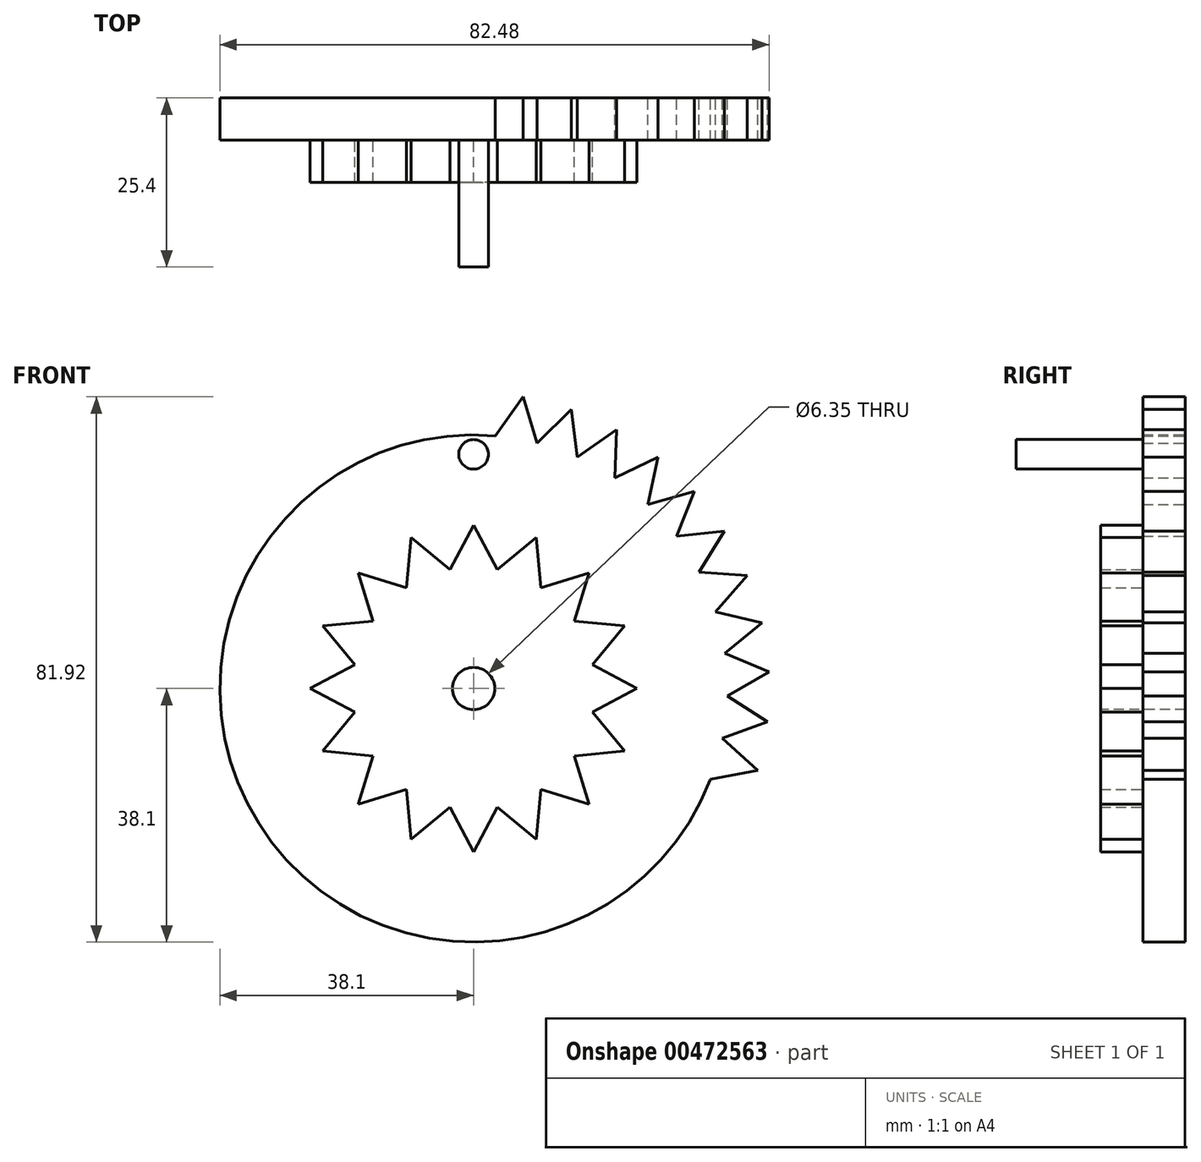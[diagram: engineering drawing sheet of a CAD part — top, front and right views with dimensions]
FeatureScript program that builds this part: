
annotation { "Feature Type Name" : "Feature", "Feature Type Description" : "" }
export const myFeature = defineFeature(function(context is Context, id is Id, definition is map)
    precondition{}
    {
        {
            var Q0;
            Q0=qCreatedBy(makeId("Front.planeOp"),FACE);
            var sketch = newSketch(context, id + "F0", { "sketchPlane" : qUnion([Q0])});
            skCircle(sketch, "E0", {"center": v(0, 0) * mm, "radius": 38.1 * mm});
            skPoint(sketch, "E1", {"position": v(0, 38.1) * mm});
            skPoint(sketch, "E2.1.0", {"position": v(6.38, 37.56) * mm});
            skPoint(sketch, "E2.2.0", {"position": v(12.58, 35.96) * mm});
            skPoint(sketch, "E2.3.0", {"position": v(18.43, 33.35) * mm});
            skPoint(sketch, "E2.4.0", {"position": v(23.75, 29.79) * mm});
            skPoint(sketch, "E2.5.0", {"position": v(28.4, 25.39) * mm});
            skPoint(sketch, "E2.6.0", {"position": v(32.26, 20.27) * mm});
            skPoint(sketch, "E2.7.0", {"position": v(35.2, 14.58) * mm});
            skPoint(sketch, "E2.8.0", {"position": v(37.14, 8.48) * mm});
            skPoint(sketch, "E2.9.0", {"position": v(38.04, 2.14) * mm});
            skPoint(sketch, "E2.10.0", {"position": v(37.86, -4.27) * mm});
            skPoint(sketch, "E2.11.0", {"position": v(36.61, -10.55) * mm});
            skPoint(sketch, "E2.12.0", {"position": v(34.33, -16.53) * mm});
            skPoint(sketch, "E2.13.0", {"position": v(31.07, -22.05) * mm});
            skPoint(sketch, "E2.14.0", {"position": v(26.94, -26.94) * mm});
            skPoint(sketch, "E2.15.0", {"position": v(22.05, -31.07) * mm});
            skPoint(sketch, "E2.16.0", {"position": v(16.53, -34.33) * mm});
            skPoint(sketch, "E2.17.0", {"position": v(10.55, -36.61) * mm});
            skPoint(sketch, "E2.18.0", {"position": v(4.27, -37.86) * mm});
            skPoint(sketch, "E2.19.0", {"position": v(-2.14, -38.04) * mm});
            skPoint(sketch, "E2.20.0", {"position": v(-8.48, -37.14) * mm});
            skPoint(sketch, "E2.21.0", {"position": v(-14.58, -35.2) * mm});
            skPoint(sketch, "E2.22.0", {"position": v(-20.27, -32.26) * mm});
            skPoint(sketch, "E2.23.0", {"position": v(-25.39, -28.4) * mm});
            skPoint(sketch, "E2.24.0", {"position": v(-29.79, -23.75) * mm});
            skPoint(sketch, "E2.25.0", {"position": v(-33.35, -18.43) * mm});
            skPoint(sketch, "E2.26.0", {"position": v(-35.96, -12.58) * mm});
            skPoint(sketch, "E2.27.0", {"position": v(-37.56, -6.38) * mm});
            skLineSegment(sketch, "E2.anchor1", {"start": v(0, 0) * mm, "end": v(0, 38.1) * mm, "construction": true});
            skLineSegment(sketch, "E2.anchor2", {"start": v(0, 0) * mm, "end": v(-38.1, 0) * mm, "construction": true});
            skPoint(sketch, "E3.0.28.0", {"position": v(-38.1, 0) * mm});
            skPoint(sketch, "E4", {"position": v(-3.17, 37.97) * mm});
            skPoint(sketch, "E5.1.0", {"position": v(3.23, 37.96) * mm});
            skPoint(sketch, "E5.2.0", {"position": v(9.55, 36.88) * mm});
            skPoint(sketch, "E5.3.0", {"position": v(15.59, 34.76) * mm});
            skPoint(sketch, "E5.4.0", {"position": v(21.2, 31.66) * mm});
            skPoint(sketch, "E5.5.0", {"position": v(26.2, 27.67) * mm});
            skPoint(sketch, "E5.6.0", {"position": v(30.46, 22.89) * mm});
            skPoint(sketch, "E5.7.0", {"position": v(33.86, 17.46) * mm});
            skPoint(sketch, "E5.8.0", {"position": v(36.3, 11.54) * mm});
            skPoint(sketch, "E5.9.0", {"position": v(37.73, 5.3) * mm});
            skPoint(sketch, "E5.10.0", {"position": v(38.08, -1.1) * mm});
            skPoint(sketch, "E5.11.0", {"position": v(37.36, -7.46) * mm});
            skPoint(sketch, "E5.12.0", {"position": v(35.58, -13.62) * mm});
            skPoint(sketch, "E5.13.0", {"position": v(32.8, -19.38) * mm});
            skPoint(sketch, "E5.14.0", {"position": v(29.1, -24.6) * mm});
            skPoint(sketch, "E5.15.0", {"position": v(24.56, -29.13) * mm});
            skPoint(sketch, "E5.16.0", {"position": v(19.33, -32.83) * mm});
            skPoint(sketch, "E5.17.0", {"position": v(13.56, -35.6) * mm});
            skPoint(sketch, "E5.18.0", {"position": v(7.4, -37.37) * mm});
            skPoint(sketch, "E5.19.0", {"position": v(1.04, -38.09) * mm});
            skPoint(sketch, "E5.20.0", {"position": v(-5.36, -37.72) * mm});
            skPoint(sketch, "E5.21.0", {"position": v(-11.6, -36.3) * mm});
            skPoint(sketch, "E5.22.0", {"position": v(-17.51, -33.84) * mm});
            skPoint(sketch, "E5.23.0", {"position": v(-22.93, -30.42) * mm});
            skPoint(sketch, "E5.24.0", {"position": v(-27.7, -26.15) * mm});
            skPoint(sketch, "E5.25.0", {"position": v(-31.7, -21.14) * mm});
            skPoint(sketch, "E5.26.0", {"position": v(-34.79, -15.53) * mm});
            skPoint(sketch, "E5.27.0", {"position": v(-36.9, -9.49) * mm});
            skPoint(sketch, "E5.28.0", {"position": v(-37.97, -3.17) * mm});
            skLineSegment(sketch, "E5.anchor1", {"start": v(0, 0) * mm, "end": v(-3.17, 37.97) * mm, "construction": true});
            skLineSegment(sketch, "E5.anchor2", {"start": v(0, 0) * mm, "end": v(-37.97, -3.17) * mm, "construction": true});
            skLineSegment(sketch, "E6", {"start": v(6.38, 37.56) * mm, "end": v(0, 0) * mm});
            skLineSegment(sketch, "E7", {"start": v(12.58, 35.96) * mm, "end": v(0, 0) * mm});
            skLineSegment(sketch, "E8", {"start": v(18.43, 33.35) * mm, "end": v(0, 0) * mm});
            skLineSegment(sketch, "E9", {"start": v(23.75, 29.79) * mm, "end": v(0, 0) * mm});
            skLineSegment(sketch, "E10", {"start": v(28.4, 25.39) * mm, "end": v(0, 0) * mm});
            skLineSegment(sketch, "E11", {"start": v(32.26, 20.27) * mm, "end": v(0, 0) * mm});
            skLineSegment(sketch, "E12", {"start": v(35.2, 14.58) * mm, "end": v(0, 0) * mm});
            skLineSegment(sketch, "E13", {"start": v(37.14, 8.48) * mm, "end": v(0, 0) * mm});
            skLineSegment(sketch, "E14", {"start": v(38.04, 2.14) * mm, "end": v(0, 0) * mm});
            skLineSegment(sketch, "E15", {"start": v(37.86, -4.27) * mm, "end": v(0, 0) * mm});
            skLineSegment(sketch, "E16", {"start": v(36.61, -10.55) * mm, "end": v(0, 0) * mm});
            skLineSegment(sketch, "E17", {"start": v(34.33, -16.53) * mm, "end": v(0, 0) * mm});
            skLineSegment(sketch, "E18", {"start": v(31.07, -22.05) * mm, "end": v(0, 0) * mm});
            skLineSegment(sketch, "E19", {"start": v(26.94, -26.94) * mm, "end": v(0, 0) * mm});
            skLineSegment(sketch, "E20", {"start": v(22.05, -31.07) * mm, "end": v(0, 0) * mm});
            skLineSegment(sketch, "E21", {"start": v(16.53, -34.33) * mm, "end": v(0, 0) * mm});
            skLineSegment(sketch, "E22", {"start": v(10.55, -36.61) * mm, "end": v(0, 0) * mm});
            skLineSegment(sketch, "E23", {"start": v(4.27, -37.86) * mm, "end": v(0, 0) * mm});
            skLineSegment(sketch, "E24", {"start": v(-2.14, -38.04) * mm, "end": v(0, 0) * mm});
            skLineSegment(sketch, "E25", {"start": v(-8.48, -37.14) * mm, "end": v(0, 0) * mm});
            skLineSegment(sketch, "E26", {"start": v(-14.58, -35.2) * mm, "end": v(0, 0) * mm});
            skLineSegment(sketch, "E27", {"start": v(-20.27, -32.26) * mm, "end": v(0, 0) * mm});
            skLineSegment(sketch, "E28", {"start": v(-25.39, -28.4) * mm, "end": v(0, 0) * mm});
            skLineSegment(sketch, "E29", {"start": v(-29.79, -23.75) * mm, "end": v(0, 0) * mm});
            skLineSegment(sketch, "E30", {"start": v(-33.35, -18.43) * mm, "end": v(0, 0) * mm});
            skLineSegment(sketch, "E31", {"start": v(-35.96, -12.58) * mm, "end": v(0, 0) * mm});
            skLineSegment(sketch, "E32", {"start": v(-37.56, -6.38) * mm, "end": v(0, 0) * mm});
            skLineSegment(sketch, "E33", {"start": v(0, 38.1) * mm, "end": v(0, 44.45) * mm});
            skLineSegment(sketch, "E34", {"start": v(6.38, 37.56) * mm, "end": v(7.45, 43.82) * mm});
            skLineSegment(sketch, "E35", {"start": v(12.58, 35.96) * mm, "end": v(14.68, 41.96) * mm});
            skLineSegment(sketch, "E36", {"start": v(18.43, 33.35) * mm, "end": v(21.5, 38.9) * mm});
            skLineSegment(sketch, "E37", {"start": v(23.75, 29.79) * mm, "end": v(27.71, 34.75) * mm});
            skLineSegment(sketch, "E38", {"start": v(28.4, 25.39) * mm, "end": v(33.14, 29.62) * mm});
            skLineSegment(sketch, "E39", {"start": v(32.26, 20.27) * mm, "end": v(37.64, 23.65) * mm});
            skLineSegment(sketch, "E40", {"start": v(35.2, 14.58) * mm, "end": v(41.07, 17.01) * mm});
            skLineSegment(sketch, "E41", {"start": v(37.14, 8.48) * mm, "end": v(43.34, 9.9) * mm});
            skLineSegment(sketch, "E42", {"start": v(38.04, 2.14) * mm, "end": v(44.38, 2.5) * mm});
            skLineSegment(sketch, "E43", {"start": v(37.86, -4.27) * mm, "end": v(44.17, -4.98) * mm});
            skLineSegment(sketch, "E44", {"start": v(36.61, -10.55) * mm, "end": v(42.71, -12.3) * mm});
            skLineSegment(sketch, "E45", {"start": v(34.33, -16.53) * mm, "end": v(40.05, -19.29) * mm});
            skLineSegment(sketch, "E46", {"start": v(31.07, -22.05) * mm, "end": v(36.25, -25.72) * mm});
            skLineSegment(sketch, "E47", {"start": v(26.94, -26.94) * mm, "end": v(31.43, -31.43) * mm});
            skLineSegment(sketch, "E48", {"start": v(22.05, -31.07) * mm, "end": v(25.72, -36.25) * mm});
            skLineSegment(sketch, "E49", {"start": v(16.53, -34.33) * mm, "end": v(19.29, -40.05) * mm});
            skLineSegment(sketch, "E50", {"start": v(10.55, -36.61) * mm, "end": v(12.3, -42.71) * mm});
            skLineSegment(sketch, "E51", {"start": v(4.27, -37.86) * mm, "end": v(4.98, -44.17) * mm});
            skLineSegment(sketch, "E52", {"start": v(-8.48, -37.14) * mm, "end": v(-9.9, -43.34) * mm});
            skLineSegment(sketch, "E53", {"start": v(-14.58, -35.2) * mm, "end": v(-17.01, -41.07) * mm});
            skLineSegment(sketch, "E54", {"start": v(-20.27, -32.26) * mm, "end": v(-23.65, -37.64) * mm});
            skLineSegment(sketch, "E55", {"start": v(-25.39, -28.4) * mm, "end": v(-29.62, -33.14) * mm});
            skLineSegment(sketch, "E56", {"start": v(-29.79, -23.75) * mm, "end": v(-34.75, -27.71) * mm});
            skLineSegment(sketch, "E57", {"start": v(-33.35, -18.43) * mm, "end": v(-38.9, -21.5) * mm});
            skLineSegment(sketch, "E58", {"start": v(-35.96, -12.58) * mm, "end": v(-41.96, -14.68) * mm});
            skLineSegment(sketch, "E59", {"start": v(-37.56, -6.38) * mm, "end": v(-43.82, -7.45) * mm});
            skLineSegment(sketch, "E60", {"start": v(-38.1, 0) * mm, "end": v(-44.45, 0) * mm});
            skLineSegment(sketch, "E61", {"start": v(-2.14, -38.04) * mm, "end": v(-2.5, -44.38) * mm});
            skLineSegment(sketch, "E62", {"start": v(0, 44.45) * mm, "end": v(-3.17, 37.97) * mm});
            skLineSegment(sketch, "E63", {"start": v(0, 44.45) * mm, "end": v(3.23, 37.96) * mm});
            skLineSegment(sketch, "E64", {"start": v(3.23, 37.96) * mm, "end": v(7.45, 43.82) * mm});
            skLineSegment(sketch, "E65", {"start": v(7.45, 43.82) * mm, "end": v(9.55, 36.88) * mm});
            skLineSegment(sketch, "E66", {"start": v(9.55, 36.88) * mm, "end": v(14.68, 41.96) * mm});
            skLineSegment(sketch, "E67", {"start": v(14.68, 41.96) * mm, "end": v(15.59, 34.76) * mm});
            skLineSegment(sketch, "E68", {"start": v(15.59, 34.76) * mm, "end": v(21.5, 38.9) * mm});
            skLineSegment(sketch, "E69", {"start": v(21.5, 38.9) * mm, "end": v(21.2, 31.66) * mm});
            skLineSegment(sketch, "E70", {"start": v(27.71, 34.75) * mm, "end": v(21.2, 31.66) * mm});
            skLineSegment(sketch, "E71", {"start": v(27.71, 34.75) * mm, "end": v(26.2, 27.67) * mm});
            skLineSegment(sketch, "E72", {"start": v(26.2, 27.67) * mm, "end": v(33.14, 29.62) * mm});
            skLineSegment(sketch, "E73", {"start": v(33.14, 29.62) * mm, "end": v(30.46, 22.89) * mm});
            skLineSegment(sketch, "E74", {"start": v(30.46, 22.89) * mm, "end": v(37.64, 23.65) * mm});
            skLineSegment(sketch, "E75", {"start": v(37.64, 23.65) * mm, "end": v(33.86, 17.46) * mm});
            skLineSegment(sketch, "E76", {"start": v(33.86, 17.46) * mm, "end": v(41.07, 17.01) * mm});
            skLineSegment(sketch, "E77", {"start": v(41.07, 17.01) * mm, "end": v(36.3, 11.54) * mm});
            skLineSegment(sketch, "E78", {"start": v(36.3, 11.54) * mm, "end": v(43.34, 9.9) * mm});
            skLineSegment(sketch, "E79", {"start": v(43.34, 9.9) * mm, "end": v(37.73, 5.3) * mm});
            skLineSegment(sketch, "E80", {"start": v(37.73, 5.3) * mm, "end": v(44.38, 2.5) * mm});
            skLineSegment(sketch, "E81", {"start": v(44.38, 2.5) * mm, "end": v(38.08, -1.1) * mm});
            skLineSegment(sketch, "E82", {"start": v(38.08, -1.1) * mm, "end": v(44.17, -4.98) * mm});
            skLineSegment(sketch, "E83", {"start": v(44.17, -4.98) * mm, "end": v(37.36, -7.46) * mm});
            skLineSegment(sketch, "E84", {"start": v(37.36, -7.46) * mm, "end": v(42.71, -12.3) * mm});
            skLineSegment(sketch, "E85", {"start": v(42.71, -12.3) * mm, "end": v(35.58, -13.62) * mm});
            skLineSegment(sketch, "E86", {"start": v(35.58, -13.62) * mm, "end": v(40.05, -19.29) * mm});
            skLineSegment(sketch, "E87", {"start": v(40.05, -19.29) * mm, "end": v(32.8, -19.38) * mm});
            skLineSegment(sketch, "E88", {"start": v(32.8, -19.38) * mm, "end": v(36.25, -25.72) * mm});
            skLineSegment(sketch, "E89", {"start": v(36.25, -25.72) * mm, "end": v(29.1, -24.6) * mm});
            skLineSegment(sketch, "E90", {"start": v(29.1, -24.6) * mm, "end": v(31.43, -31.43) * mm});
            skLineSegment(sketch, "E91", {"start": v(31.43, -31.43) * mm, "end": v(24.56, -29.13) * mm});
            skLineSegment(sketch, "E92", {"start": v(24.56, -29.13) * mm, "end": v(25.72, -36.25) * mm});
            skLineSegment(sketch, "E93", {"start": v(25.72, -36.25) * mm, "end": v(19.33, -32.83) * mm});
            skLineSegment(sketch, "E94", {"start": v(19.33, -32.83) * mm, "end": v(19.29, -40.05) * mm});
            skLineSegment(sketch, "E95", {"start": v(19.29, -40.05) * mm, "end": v(13.56, -35.6) * mm});
            skLineSegment(sketch, "E96", {"start": v(13.56, -35.6) * mm, "end": v(12.3, -42.71) * mm});
            skLineSegment(sketch, "E97", {"start": v(12.3, -42.71) * mm, "end": v(7.4, -37.37) * mm});
            skLineSegment(sketch, "E98", {"start": v(7.4, -37.37) * mm, "end": v(4.98, -44.17) * mm});
            skLineSegment(sketch, "E99", {"start": v(4.98, -44.17) * mm, "end": v(1.04, -38.09) * mm});
            skLineSegment(sketch, "E100", {"start": v(1.04, -38.09) * mm, "end": v(-2.5, -44.38) * mm});
            skLineSegment(sketch, "E101", {"start": v(-2.5, -44.38) * mm, "end": v(-5.36, -37.72) * mm});
            skLineSegment(sketch, "E102", {"start": v(-5.36, -37.72) * mm, "end": v(-9.9, -43.34) * mm});
            skLineSegment(sketch, "E103", {"start": v(-9.9, -43.34) * mm, "end": v(-11.6, -36.3) * mm});
            skLineSegment(sketch, "E104", {"start": v(-11.6, -36.3) * mm, "end": v(-17.01, -41.07) * mm});
            skLineSegment(sketch, "E105", {"start": v(-17.01, -41.07) * mm, "end": v(-17.51, -33.84) * mm});
            skLineSegment(sketch, "E106", {"start": v(-17.51, -33.84) * mm, "end": v(-23.65, -37.64) * mm});
            skLineSegment(sketch, "E107", {"start": v(-23.65, -37.64) * mm, "end": v(-22.93, -30.42) * mm});
            skLineSegment(sketch, "E108", {"start": v(-22.93, -30.42) * mm, "end": v(-29.62, -33.14) * mm});
            skLineSegment(sketch, "E109", {"start": v(-29.62, -33.14) * mm, "end": v(-27.7, -26.15) * mm});
            skLineSegment(sketch, "E110", {"start": v(-27.7, -26.15) * mm, "end": v(-34.75, -27.71) * mm});
            skLineSegment(sketch, "E111", {"start": v(-34.75, -27.71) * mm, "end": v(-31.7, -21.14) * mm});
            skLineSegment(sketch, "E112", {"start": v(-31.7, -21.14) * mm, "end": v(-38.9, -21.5) * mm});
            skLineSegment(sketch, "E113", {"start": v(-34.79, -15.53) * mm, "end": v(-38.9, -21.5) * mm});
            skLineSegment(sketch, "E114", {"start": v(-41.96, -14.68) * mm, "end": v(-34.79, -15.53) * mm});
            skLineSegment(sketch, "E115", {"start": v(-36.9, -9.49) * mm, "end": v(-41.96, -14.68) * mm});
            skLineSegment(sketch, "E116", {"start": v(-36.9, -9.49) * mm, "end": v(-43.82, -7.45) * mm});
            skLineSegment(sketch, "E117", {"start": v(-43.82, -7.45) * mm, "end": v(-37.97, -3.17) * mm});
            skLineSegment(sketch, "E118", {"start": v(-37.97, -3.17) * mm, "end": v(-44.45, 0) * mm});
            skPoint(sketch, "E119", {"position": v(-37.97, 3.17) * mm});
            skLineSegment(sketch, "E120", {"start": v(-44.45, 0) * mm, "end": v(-37.97, 3.17) * mm});
            skSolve(sketch);
        }
        {
            var Q0;
            Q0=qSketchRegion(id+"F0",true);
            extrude(context, id + "F1", {"entities" : qUnion([Q0]), "depth" : 6.35 * mm});
        }
        {
            var Q0;
            Q0=makeQuery(id+"F1.opExtrude","CAP_FACE",FACE,{"disambiguationData":[OSD([sQuery(id+"F0.wireOp",EDGE,"E0"),sQuery(id+"F0.wireOp",EDGE,"E62"),sQuery(id+"F0.wireOp",EDGE,"E63"),sQuery(id+"F0.wireOp",EDGE,"E64"),sQuery(id+"F0.wireOp",EDGE,"E65"),sQuery(id+"F0.wireOp",EDGE,"E66"),sQuery(id+"F0.wireOp",EDGE,"E67"),sQuery(id+"F0.wireOp",EDGE,"E68"),sQuery(id+"F0.wireOp",EDGE,"E69"),sQuery(id+"F0.wireOp",EDGE,"E70"),sQuery(id+"F0.wireOp",EDGE,"E71"),sQuery(id+"F0.wireOp",EDGE,"E72"),sQuery(id+"F0.wireOp",EDGE,"E73"),sQuery(id+"F0.wireOp",EDGE,"E74"),sQuery(id+"F0.wireOp",EDGE,"E75"),sQuery(id+"F0.wireOp",EDGE,"E76"),sQuery(id+"F0.wireOp",EDGE,"E77"),sQuery(id+"F0.wireOp",EDGE,"E78"),sQuery(id+"F0.wireOp",EDGE,"E79"),sQuery(id+"F0.wireOp",EDGE,"E80"),sQuery(id+"F0.wireOp",EDGE,"E81"),sQuery(id+"F0.wireOp",EDGE,"E82"),sQuery(id+"F0.wireOp",EDGE,"E83"),sQuery(id+"F0.wireOp",EDGE,"E84"),sQuery(id+"F0.wireOp",EDGE,"E85"),sQuery(id+"F0.wireOp",EDGE,"E86"),sQuery(id+"F0.wireOp",EDGE,"E87"),sQuery(id+"F0.wireOp",EDGE,"E88"),sQuery(id+"F0.wireOp",EDGE,"E89"),sQuery(id+"F0.wireOp",EDGE,"E90"),sQuery(id+"F0.wireOp",EDGE,"E91"),sQuery(id+"F0.wireOp",EDGE,"E92"),sQuery(id+"F0.wireOp",EDGE,"E93"),sQuery(id+"F0.wireOp",EDGE,"E94"),sQuery(id+"F0.wireOp",EDGE,"E95"),sQuery(id+"F0.wireOp",EDGE,"E96"),sQuery(id+"F0.wireOp",EDGE,"E97"),sQuery(id+"F0.wireOp",EDGE,"E98"),sQuery(id+"F0.wireOp",EDGE,"E99"),sQuery(id+"F0.wireOp",EDGE,"E100"),sQuery(id+"F0.wireOp",EDGE,"E101"),sQuery(id+"F0.wireOp",EDGE,"E102"),sQuery(id+"F0.wireOp",EDGE,"E103"),sQuery(id+"F0.wireOp",EDGE,"E104"),sQuery(id+"F0.wireOp",EDGE,"E105"),sQuery(id+"F0.wireOp",EDGE,"E106"),sQuery(id+"F0.wireOp",EDGE,"E107"),sQuery(id+"F0.wireOp",EDGE,"E108"),sQuery(id+"F0.wireOp",EDGE,"E109"),sQuery(id+"F0.wireOp",EDGE,"E110"),sQuery(id+"F0.wireOp",EDGE,"E111"),sQuery(id+"F0.wireOp",EDGE,"E112"),sQuery(id+"F0.wireOp",EDGE,"E113"),sQuery(id+"F0.wireOp",EDGE,"E114"),sQuery(id+"F0.wireOp",EDGE,"E115"),sQuery(id+"F0.wireOp",EDGE,"E116"),sQuery(id+"F0.wireOp",EDGE,"E117"),sQuery(id+"F0.wireOp",EDGE,"E118"),sQuery(id+"F0.wireOp",EDGE,"E120")])],"isStart":false});
            var sketch = newSketch(context, id + "F2", { "sketchPlane" : qUnion([Q0])});
            skPoint(sketch, "E121", {"position": v(0, 35.18) * mm});
            skCircle(sketch, "E122", {"center": v(0, 35.18) * mm, "radius": 2.22 * mm});
            skSolve(sketch);
        }
        {
            var Q0;
            Q0=makeQuery(id+"F2.imprint","IMPRINT",FACE,{"disambiguationData":[TD([[makeQuery(id+"F2.imprint","IMPRINT",EDGE,{"derivedFrom":sQuery(id+"F2.wireOp",EDGE,"E122")}),1.0]])]});
            extrude(context, id + "F3", {"entities" : qUnion([Q0]), "operationType" : NewBodyOperationType.ADD, "depth" : 19.05 * mm});
        }
        {
            var Q0;
            Q0=makeQuery(id+"F1.opExtrude","CAP_FACE",FACE,{"disambiguationData":[OSD([sQuery(id+"F0.wireOp",EDGE,"E0"),sQuery(id+"F0.wireOp",EDGE,"E62"),sQuery(id+"F0.wireOp",EDGE,"E63"),sQuery(id+"F0.wireOp",EDGE,"E64"),sQuery(id+"F0.wireOp",EDGE,"E65"),sQuery(id+"F0.wireOp",EDGE,"E66"),sQuery(id+"F0.wireOp",EDGE,"E67"),sQuery(id+"F0.wireOp",EDGE,"E68"),sQuery(id+"F0.wireOp",EDGE,"E69"),sQuery(id+"F0.wireOp",EDGE,"E70"),sQuery(id+"F0.wireOp",EDGE,"E71"),sQuery(id+"F0.wireOp",EDGE,"E72"),sQuery(id+"F0.wireOp",EDGE,"E73"),sQuery(id+"F0.wireOp",EDGE,"E74"),sQuery(id+"F0.wireOp",EDGE,"E75"),sQuery(id+"F0.wireOp",EDGE,"E76"),sQuery(id+"F0.wireOp",EDGE,"E77"),sQuery(id+"F0.wireOp",EDGE,"E78"),sQuery(id+"F0.wireOp",EDGE,"E79"),sQuery(id+"F0.wireOp",EDGE,"E80"),sQuery(id+"F0.wireOp",EDGE,"E81"),sQuery(id+"F0.wireOp",EDGE,"E82"),sQuery(id+"F0.wireOp",EDGE,"E83"),sQuery(id+"F0.wireOp",EDGE,"E84"),sQuery(id+"F0.wireOp",EDGE,"E85"),sQuery(id+"F0.wireOp",EDGE,"E86"),sQuery(id+"F0.wireOp",EDGE,"E87"),sQuery(id+"F0.wireOp",EDGE,"E88"),sQuery(id+"F0.wireOp",EDGE,"E89"),sQuery(id+"F0.wireOp",EDGE,"E90"),sQuery(id+"F0.wireOp",EDGE,"E91"),sQuery(id+"F0.wireOp",EDGE,"E92"),sQuery(id+"F0.wireOp",EDGE,"E93"),sQuery(id+"F0.wireOp",EDGE,"E94"),sQuery(id+"F0.wireOp",EDGE,"E95"),sQuery(id+"F0.wireOp",EDGE,"E96"),sQuery(id+"F0.wireOp",EDGE,"E97"),sQuery(id+"F0.wireOp",EDGE,"E98"),sQuery(id+"F0.wireOp",EDGE,"E99"),sQuery(id+"F0.wireOp",EDGE,"E100"),sQuery(id+"F0.wireOp",EDGE,"E101"),sQuery(id+"F0.wireOp",EDGE,"E102"),sQuery(id+"F0.wireOp",EDGE,"E103"),sQuery(id+"F0.wireOp",EDGE,"E104"),sQuery(id+"F0.wireOp",EDGE,"E105"),sQuery(id+"F0.wireOp",EDGE,"E106"),sQuery(id+"F0.wireOp",EDGE,"E107"),sQuery(id+"F0.wireOp",EDGE,"E108"),sQuery(id+"F0.wireOp",EDGE,"E109"),sQuery(id+"F0.wireOp",EDGE,"E110"),sQuery(id+"F0.wireOp",EDGE,"E111"),sQuery(id+"F0.wireOp",EDGE,"E112"),sQuery(id+"F0.wireOp",EDGE,"E113"),sQuery(id+"F0.wireOp",EDGE,"E114"),sQuery(id+"F0.wireOp",EDGE,"E115"),sQuery(id+"F0.wireOp",EDGE,"E116"),sQuery(id+"F0.wireOp",EDGE,"E117"),sQuery(id+"F0.wireOp",EDGE,"E118"),sQuery(id+"F0.wireOp",EDGE,"E120")])],"isStart":false});
            var sketch = newSketch(context, id + "F4", { "sketchPlane" : qUnion([Q0])});
            skCircle(sketch, "E123", {"center": v(0, 0) * mm, "radius": 38.1 * mm});
            skPoint(sketch, "E124", {"position": v(3.23, 37.96) * mm});
            skPoint(sketch, "E125", {"position": v(35.58, -13.62) * mm});
            skLineSegment(sketch, "E126", {"start": v(3.23, 37.96) * mm, "end": v(3.23, 56.1) * mm});
            skLineSegment(sketch, "E127", {"start": v(35.58, -13.62) * mm, "end": v(52.43, -20.2) * mm});
            skArc(sketch, "E128", {"start": v(3.23, 56.1) * mm, "mid": v(-47.22, -30.45) * mm, "end": v(52.43, -20.2) * mm});
            skSolve(sketch);
        }
        {
            var Q0;
            Q0=makeQuery(id+"F4.imprint","IMPRINT",FACE,{"disambiguationData":[TD([[makeQuery(id+"F4.imprint","IMPRINT",EDGE,{"derivedFrom":makeQuery(id+"F9.boolean.opBoolean","COPY",EDGE,{"derivedFrom":makeQuery(id+"F9.opExtrude","CAP_EDGE",EDGE,{"disambiguationData":[OSD([sQuery(id+"F8.wireOp",EDGE,"E195")])],"isStart":true})})}),1.0]])]});
            var Q1;
            Q1=makeQuery(id+"F4.imprint","IMPRINT",FACE,{"disambiguationData":[TD([[makeQuery(id+"F4.imprint","IMPRINT",EDGE,{"derivedFrom":makeQuery(id+"F3.opExtrude","CAP_EDGE",EDGE,{"disambiguationData":[OSD([sQuery(id+"F2.wireOp",EDGE,"E122")])],"isStart":true})}),1.0]])]});
            var Q2;
            {var subQ1=makeQuery(id+"F1.opExtrude","CAP_EDGE",EDGE,{"disambiguationData":[OSD([sQuery(id+"F0.wireOp",EDGE,"E62")])],"isStart":false});Q2=makeQuery(id+"F4.imprint","IMPRINT",FACE,{"disambiguationData":[TD([[makeQuery(id+"F4.imprint","IMPRINT",EDGE,{"derivedFrom":subQ1}),1.0]])]});}
            var Q3;
            {var subQ1=makeQuery(id+"F1.opExtrude","CAP_EDGE",EDGE,{"disambiguationData":[OSD([sQuery(id+"F0.wireOp",EDGE,"E118")])],"isStart":false});Q3=makeQuery(id+"F4.imprint","IMPRINT",FACE,{"disambiguationData":[TD([[makeQuery(id+"F4.imprint","IMPRINT",EDGE,{"derivedFrom":subQ1}),-1.0]])]});}
            var Q4;
            {var subQ1=makeQuery(id+"F1.opExtrude","CAP_EDGE",EDGE,{"disambiguationData":[OSD([sQuery(id+"F0.wireOp",EDGE,"E116")])],"isStart":false});Q4=makeQuery(id+"F4.imprint","IMPRINT",FACE,{"disambiguationData":[TD([[makeQuery(id+"F4.imprint","IMPRINT",EDGE,{"derivedFrom":subQ1}),-1.0]])]});}
            var Q5;
            {var subQ1=makeQuery(id+"F1.opExtrude","CAP_EDGE",EDGE,{"disambiguationData":[OSD([sQuery(id+"F0.wireOp",EDGE,"E114")])],"isStart":false});Q5=makeQuery(id+"F4.imprint","IMPRINT",FACE,{"disambiguationData":[TD([[makeQuery(id+"F4.imprint","IMPRINT",EDGE,{"derivedFrom":subQ1}),1.0]])]});}
            var Q6;
            {var subQ1=makeQuery(id+"F1.opExtrude","CAP_EDGE",EDGE,{"disambiguationData":[OSD([sQuery(id+"F0.wireOp",EDGE,"E112")])],"isStart":false});Q6=makeQuery(id+"F4.imprint","IMPRINT",FACE,{"disambiguationData":[TD([[makeQuery(id+"F4.imprint","IMPRINT",EDGE,{"derivedFrom":subQ1}),-1.0]])]});}
            var Q7;
            {var subQ1=makeQuery(id+"F1.opExtrude","CAP_EDGE",EDGE,{"disambiguationData":[OSD([sQuery(id+"F0.wireOp",EDGE,"E110")])],"isStart":false});Q7=makeQuery(id+"F4.imprint","IMPRINT",FACE,{"disambiguationData":[TD([[makeQuery(id+"F4.imprint","IMPRINT",EDGE,{"derivedFrom":subQ1}),-1.0]])]});}
            var Q8;
            {var subQ1=makeQuery(id+"F1.opExtrude","CAP_EDGE",EDGE,{"disambiguationData":[OSD([sQuery(id+"F0.wireOp",EDGE,"E108")])],"isStart":false});Q8=makeQuery(id+"F4.imprint","IMPRINT",FACE,{"disambiguationData":[TD([[makeQuery(id+"F4.imprint","IMPRINT",EDGE,{"derivedFrom":subQ1}),-1.0]])]});}
            var Q9;
            {var subQ1=makeQuery(id+"F1.opExtrude","CAP_EDGE",EDGE,{"disambiguationData":[OSD([sQuery(id+"F0.wireOp",EDGE,"E106")])],"isStart":false});Q9=makeQuery(id+"F4.imprint","IMPRINT",FACE,{"disambiguationData":[TD([[makeQuery(id+"F4.imprint","IMPRINT",EDGE,{"derivedFrom":subQ1}),-1.0]])]});}
            var Q10;
            {var subQ1=makeQuery(id+"F1.opExtrude","CAP_EDGE",EDGE,{"disambiguationData":[OSD([sQuery(id+"F0.wireOp",EDGE,"E104")])],"isStart":false});Q10=makeQuery(id+"F4.imprint","IMPRINT",FACE,{"disambiguationData":[TD([[makeQuery(id+"F4.imprint","IMPRINT",EDGE,{"derivedFrom":subQ1}),-1.0]])]});}
            var Q11;
            {var subQ1=makeQuery(id+"F1.opExtrude","CAP_EDGE",EDGE,{"disambiguationData":[OSD([sQuery(id+"F0.wireOp",EDGE,"E102")])],"isStart":false});Q11=makeQuery(id+"F4.imprint","IMPRINT",FACE,{"disambiguationData":[TD([[makeQuery(id+"F4.imprint","IMPRINT",EDGE,{"derivedFrom":subQ1}),-1.0]])]});}
            var Q12;
            {var subQ1=makeQuery(id+"F1.opExtrude","CAP_EDGE",EDGE,{"disambiguationData":[OSD([sQuery(id+"F0.wireOp",EDGE,"E100")])],"isStart":false});Q12=makeQuery(id+"F4.imprint","IMPRINT",FACE,{"disambiguationData":[TD([[makeQuery(id+"F4.imprint","IMPRINT",EDGE,{"derivedFrom":subQ1}),-1.0]])]});}
            var Q13;
            {var subQ1=makeQuery(id+"F1.opExtrude","CAP_EDGE",EDGE,{"disambiguationData":[OSD([sQuery(id+"F0.wireOp",EDGE,"E98")])],"isStart":false});Q13=makeQuery(id+"F4.imprint","IMPRINT",FACE,{"disambiguationData":[TD([[makeQuery(id+"F4.imprint","IMPRINT",EDGE,{"derivedFrom":subQ1}),-1.0]])]});}
            var Q14;
            {var subQ1=makeQuery(id+"F1.opExtrude","CAP_EDGE",EDGE,{"disambiguationData":[OSD([sQuery(id+"F0.wireOp",EDGE,"E96")])],"isStart":false});Q14=makeQuery(id+"F4.imprint","IMPRINT",FACE,{"disambiguationData":[TD([[makeQuery(id+"F4.imprint","IMPRINT",EDGE,{"derivedFrom":subQ1}),-1.0]])]});}
            var Q15;
            {var subQ1=makeQuery(id+"F1.opExtrude","CAP_EDGE",EDGE,{"disambiguationData":[OSD([sQuery(id+"F0.wireOp",EDGE,"E94")])],"isStart":false});Q15=makeQuery(id+"F4.imprint","IMPRINT",FACE,{"disambiguationData":[TD([[makeQuery(id+"F4.imprint","IMPRINT",EDGE,{"derivedFrom":subQ1}),-1.0]])]});}
            var Q16;
            {var subQ1=makeQuery(id+"F1.opExtrude","CAP_EDGE",EDGE,{"disambiguationData":[OSD([sQuery(id+"F0.wireOp",EDGE,"E92")])],"isStart":false});Q16=makeQuery(id+"F4.imprint","IMPRINT",FACE,{"disambiguationData":[TD([[makeQuery(id+"F4.imprint","IMPRINT",EDGE,{"derivedFrom":subQ1}),-1.0]])]});}
            var Q17;
            {var subQ1=makeQuery(id+"F1.opExtrude","CAP_EDGE",EDGE,{"disambiguationData":[OSD([sQuery(id+"F0.wireOp",EDGE,"E90")])],"isStart":false});Q17=makeQuery(id+"F4.imprint","IMPRINT",FACE,{"disambiguationData":[TD([[makeQuery(id+"F4.imprint","IMPRINT",EDGE,{"derivedFrom":subQ1}),-1.0]])]});}
            var Q18;
            {var subQ1=makeQuery(id+"F1.opExtrude","CAP_EDGE",EDGE,{"disambiguationData":[OSD([sQuery(id+"F0.wireOp",EDGE,"E88")])],"isStart":false});Q18=makeQuery(id+"F4.imprint","IMPRINT",FACE,{"disambiguationData":[TD([[makeQuery(id+"F4.imprint","IMPRINT",EDGE,{"derivedFrom":subQ1}),-1.0]])]});}
            var Q19;
            {var subQ1=makeQuery(id+"F1.opExtrude","CAP_EDGE",EDGE,{"disambiguationData":[OSD([sQuery(id+"F0.wireOp",EDGE,"E86")])],"isStart":false});Q19=makeQuery(id+"F4.imprint","IMPRINT",FACE,{"disambiguationData":[TD([[makeQuery(id+"F4.imprint","IMPRINT",EDGE,{"derivedFrom":subQ1}),-1.0]])]});}
            var Q20;
            Q20=makeQuery(id+"F4.imprint","IMPRINT",FACE,{"disambiguationData":[TD([[makeQuery(id+"F4.imprint","IMPRINT",EDGE,{"derivedFrom":sQuery(id+"F4.wireOp",EDGE,"E126")}),1.0]])]});
            extrude(context, id + "F5", {"entities" : qUnion([Q0, Q1, Q2, Q3, Q4, Q5, Q6, Q7, Q8, Q9, Q10, Q11, Q12, Q13, Q14, Q15, Q16, Q17, Q18, Q19, Q20]), "operationType" : NewBodyOperationType.REMOVE, "oppositeDirection" : true, "depth" : 25.4 * mm});
        }
        {
            var Q0;
            Q0=makeQuery(id+"F1.opExtrude","CAP_FACE",FACE,{"disambiguationData":[OSD([sQuery(id+"F0.wireOp",EDGE,"E0"),sQuery(id+"F0.wireOp",EDGE,"E62"),sQuery(id+"F0.wireOp",EDGE,"E63"),sQuery(id+"F0.wireOp",EDGE,"E64"),sQuery(id+"F0.wireOp",EDGE,"E65"),sQuery(id+"F0.wireOp",EDGE,"E66"),sQuery(id+"F0.wireOp",EDGE,"E67"),sQuery(id+"F0.wireOp",EDGE,"E68"),sQuery(id+"F0.wireOp",EDGE,"E69"),sQuery(id+"F0.wireOp",EDGE,"E70"),sQuery(id+"F0.wireOp",EDGE,"E71"),sQuery(id+"F0.wireOp",EDGE,"E72"),sQuery(id+"F0.wireOp",EDGE,"E73"),sQuery(id+"F0.wireOp",EDGE,"E74"),sQuery(id+"F0.wireOp",EDGE,"E75"),sQuery(id+"F0.wireOp",EDGE,"E76"),sQuery(id+"F0.wireOp",EDGE,"E77"),sQuery(id+"F0.wireOp",EDGE,"E78"),sQuery(id+"F0.wireOp",EDGE,"E79"),sQuery(id+"F0.wireOp",EDGE,"E80"),sQuery(id+"F0.wireOp",EDGE,"E81"),sQuery(id+"F0.wireOp",EDGE,"E82"),sQuery(id+"F0.wireOp",EDGE,"E83"),sQuery(id+"F0.wireOp",EDGE,"E84"),sQuery(id+"F0.wireOp",EDGE,"E85"),sQuery(id+"F0.wireOp",EDGE,"E86"),sQuery(id+"F0.wireOp",EDGE,"E87"),sQuery(id+"F0.wireOp",EDGE,"E88"),sQuery(id+"F0.wireOp",EDGE,"E89"),sQuery(id+"F0.wireOp",EDGE,"E90"),sQuery(id+"F0.wireOp",EDGE,"E91"),sQuery(id+"F0.wireOp",EDGE,"E92"),sQuery(id+"F0.wireOp",EDGE,"E93"),sQuery(id+"F0.wireOp",EDGE,"E94"),sQuery(id+"F0.wireOp",EDGE,"E95"),sQuery(id+"F0.wireOp",EDGE,"E96"),sQuery(id+"F0.wireOp",EDGE,"E97"),sQuery(id+"F0.wireOp",EDGE,"E98"),sQuery(id+"F0.wireOp",EDGE,"E99"),sQuery(id+"F0.wireOp",EDGE,"E100"),sQuery(id+"F0.wireOp",EDGE,"E101"),sQuery(id+"F0.wireOp",EDGE,"E102"),sQuery(id+"F0.wireOp",EDGE,"E103"),sQuery(id+"F0.wireOp",EDGE,"E104"),sQuery(id+"F0.wireOp",EDGE,"E105"),sQuery(id+"F0.wireOp",EDGE,"E106"),sQuery(id+"F0.wireOp",EDGE,"E107"),sQuery(id+"F0.wireOp",EDGE,"E108"),sQuery(id+"F0.wireOp",EDGE,"E109"),sQuery(id+"F0.wireOp",EDGE,"E110"),sQuery(id+"F0.wireOp",EDGE,"E111"),sQuery(id+"F0.wireOp",EDGE,"E112"),sQuery(id+"F0.wireOp",EDGE,"E113"),sQuery(id+"F0.wireOp",EDGE,"E114"),sQuery(id+"F0.wireOp",EDGE,"E115"),sQuery(id+"F0.wireOp",EDGE,"E116"),sQuery(id+"F0.wireOp",EDGE,"E117"),sQuery(id+"F0.wireOp",EDGE,"E118"),sQuery(id+"F0.wireOp",EDGE,"E120")])],"isStart":false});
            var sketch = newSketch(context, id + "F6", { "sketchPlane" : qUnion([Q0])});
            skCircle(sketch, "E129", {"center": v(0, 0) * mm, "radius": 18.2 * mm});
            skPoint(sketch, "E130", {"position": v(0, 18.2) * mm});
            skPoint(sketch, "E131.1.0", {"position": v(3.55, 17.84) * mm});
            skPoint(sketch, "E131.2.0", {"position": v(6.96, 16.8) * mm});
            skPoint(sketch, "E131.3.0", {"position": v(10.1, 15.13) * mm});
            skPoint(sketch, "E131.4.0", {"position": v(12.86, 12.86) * mm});
            skPoint(sketch, "E131.5.0", {"position": v(15.13, 10.1) * mm});
            skPoint(sketch, "E131.6.0", {"position": v(16.8, 6.96) * mm});
            skPoint(sketch, "E131.7.0", {"position": v(17.84, 3.55) * mm});
            skPoint(sketch, "E131.8.0", {"position": v(18.2, 0) * mm});
            skLineSegment(sketch, "E131.anchor1", {"start": v(0, 0) * mm, "end": v(0, 18.2) * mm, "construction": true});
            skLineSegment(sketch, "E131.anchor2", {"start": v(0, 0) * mm, "end": v(18.2, 0) * mm, "construction": true});
            skPoint(sketch, "E132.1.0", {"position": v(17.84, -3.55) * mm});
            skPoint(sketch, "E132.2.0", {"position": v(16.8, -6.96) * mm});
            skPoint(sketch, "E132.3.0", {"position": v(15.13, -10.1) * mm});
            skPoint(sketch, "E132.4.0", {"position": v(12.86, -12.86) * mm});
            skPoint(sketch, "E132.5.0", {"position": v(10.1, -15.13) * mm});
            skPoint(sketch, "E132.6.0", {"position": v(6.96, -16.8) * mm});
            skPoint(sketch, "E132.7.0", {"position": v(3.55, -17.84) * mm});
            skPoint(sketch, "E132.8.0", {"position": v(0, -18.2) * mm});
            skLineSegment(sketch, "E132.anchor2", {"start": v(0, 0) * mm, "end": v(0, -18.2) * mm, "construction": true});
            skPoint(sketch, "E133.1.0", {"position": v(-3.55, -17.84) * mm});
            skPoint(sketch, "E133.2.0", {"position": v(-6.96, -16.8) * mm});
            skPoint(sketch, "E133.3.0", {"position": v(-10.1, -15.13) * mm});
            skPoint(sketch, "E133.4.0", {"position": v(-12.86, -12.86) * mm});
            skPoint(sketch, "E133.5.0", {"position": v(-15.13, -10.1) * mm});
            skPoint(sketch, "E133.6.0", {"position": v(-16.8, -6.96) * mm});
            skPoint(sketch, "E133.7.0", {"position": v(-17.84, -3.55) * mm});
            skPoint(sketch, "E133.8.0", {"position": v(-18.2, 0) * mm});
            skLineSegment(sketch, "E133.anchor2", {"start": v(0, 0) * mm, "end": v(-18.2, 0) * mm, "construction": true});
            skPoint(sketch, "E134.1.0", {"position": v(-17.84, 3.55) * mm});
            skPoint(sketch, "E134.2.0", {"position": v(-16.8, 6.96) * mm});
            skPoint(sketch, "E134.3.0", {"position": v(-15.13, 10.1) * mm});
            skPoint(sketch, "E134.4.0", {"position": v(-12.86, 12.86) * mm});
            skPoint(sketch, "E134.5.0", {"position": v(-10.1, 15.13) * mm});
            skPoint(sketch, "E134.6.0", {"position": v(-6.96, 16.8) * mm});
            skPoint(sketch, "E134.7.0", {"position": v(-3.55, 17.84) * mm});
            skLineSegment(sketch, "E135", {"start": v(0, 18.2) * mm, "end": v(0, 24.54) * mm});
            skLineSegment(sketch, "E136", {"start": v(0, 0) * mm, "end": v(6.96, 16.8) * mm});
            skLineSegment(sketch, "E137", {"start": v(0, 0) * mm, "end": v(12.86, 12.86) * mm});
            skLineSegment(sketch, "E138", {"start": v(0, 0) * mm, "end": v(16.8, 6.96) * mm});
            skLineSegment(sketch, "E139", {"start": v(0, 0) * mm, "end": v(16.8, -6.96) * mm});
            skLineSegment(sketch, "E140", {"start": v(0, 0) * mm, "end": v(12.86, -12.86) * mm});
            skLineSegment(sketch, "E141", {"start": v(0, 0) * mm, "end": v(6.96, -16.8) * mm});
            skLineSegment(sketch, "E142", {"start": v(0, 0) * mm, "end": v(-6.96, -16.8) * mm});
            skLineSegment(sketch, "E143", {"start": v(0, 0) * mm, "end": v(-12.86, -12.86) * mm});
            skLineSegment(sketch, "E144", {"start": v(0, 0) * mm, "end": v(-16.8, -6.96) * mm});
            skLineSegment(sketch, "E145", {"start": v(0, 0) * mm, "end": v(-16.8, 6.96) * mm});
            skLineSegment(sketch, "E146", {"start": v(0, 0) * mm, "end": v(-12.86, 12.86) * mm});
            skLineSegment(sketch, "E147", {"start": v(0, 0) * mm, "end": v(-6.96, 16.8) * mm});
            skLineSegment(sketch, "E148", {"start": v(6.96, 16.8) * mm, "end": v(9.4, 22.67) * mm});
            skLineSegment(sketch, "E149", {"start": v(12.86, 12.86) * mm, "end": v(17.35, 17.35) * mm});
            skLineSegment(sketch, "E150", {"start": v(16.8, 6.96) * mm, "end": v(22.67, 9.4) * mm});
            skLineSegment(sketch, "E151", {"start": v(18.2, 0) * mm, "end": v(24.54, 0) * mm});
            skLineSegment(sketch, "E152", {"start": v(16.8, -6.96) * mm, "end": v(22.67, -9.4) * mm});
            skLineSegment(sketch, "E153", {"start": v(12.86, -12.86) * mm, "end": v(17.35, -17.35) * mm});
            skLineSegment(sketch, "E154", {"start": v(6.96, -16.8) * mm, "end": v(9.4, -22.67) * mm});
            skLineSegment(sketch, "E155", {"start": v(0, -18.2) * mm, "end": v(0, -24.54) * mm});
            skLineSegment(sketch, "E156", {"start": v(-6.96, -16.8) * mm, "end": v(-9.4, -22.67) * mm});
            skLineSegment(sketch, "E157", {"start": v(-12.86, -12.86) * mm, "end": v(-17.35, -17.35) * mm});
            skLineSegment(sketch, "E158", {"start": v(-16.8, -6.96) * mm, "end": v(-22.67, -9.4) * mm});
            skLineSegment(sketch, "E159", {"start": v(-18.2, 0) * mm, "end": v(-24.54, 0) * mm});
            skLineSegment(sketch, "E160", {"start": v(-16.8, 6.96) * mm, "end": v(-22.67, 9.4) * mm});
            skLineSegment(sketch, "E161", {"start": v(-12.86, 12.86) * mm, "end": v(-17.35, 17.35) * mm});
            skLineSegment(sketch, "E162", {"start": v(-6.96, 16.8) * mm, "end": v(-9.4, 22.67) * mm});
            skLineSegment(sketch, "E163", {"start": v(0, 24.54) * mm, "end": v(3.55, 17.84) * mm});
            skLineSegment(sketch, "E164", {"start": v(3.55, 17.84) * mm, "end": v(9.4, 22.67) * mm});
            skLineSegment(sketch, "E165", {"start": v(9.4, 22.67) * mm, "end": v(10.1, 15.13) * mm});
            skLineSegment(sketch, "E166", {"start": v(10.1, 15.13) * mm, "end": v(17.35, 17.35) * mm});
            skLineSegment(sketch, "E167", {"start": v(17.35, 17.35) * mm, "end": v(15.13, 10.1) * mm});
            skLineSegment(sketch, "E168", {"start": v(15.13, 10.1) * mm, "end": v(22.67, 9.4) * mm});
            skLineSegment(sketch, "E169", {"start": v(22.67, 9.4) * mm, "end": v(17.84, 3.55) * mm});
            skLineSegment(sketch, "E170", {"start": v(17.84, 3.55) * mm, "end": v(24.54, 0) * mm});
            skLineSegment(sketch, "E171", {"start": v(24.54, 0) * mm, "end": v(17.84, -3.55) * mm});
            skLineSegment(sketch, "E172", {"start": v(17.84, -3.55) * mm, "end": v(22.67, -9.4) * mm});
            skLineSegment(sketch, "E173", {"start": v(22.67, -9.4) * mm, "end": v(15.13, -10.1) * mm});
            skLineSegment(sketch, "E174", {"start": v(15.13, -10.1) * mm, "end": v(17.35, -17.35) * mm});
            skLineSegment(sketch, "E175", {"start": v(17.35, -17.35) * mm, "end": v(10.1, -15.13) * mm});
            skLineSegment(sketch, "E176", {"start": v(10.1, -15.13) * mm, "end": v(9.4, -22.67) * mm});
            skLineSegment(sketch, "E177", {"start": v(9.4, -22.67) * mm, "end": v(3.55, -17.84) * mm});
            skLineSegment(sketch, "E178", {"start": v(3.55, -17.84) * mm, "end": v(0, -24.54) * mm});
            skLineSegment(sketch, "E179", {"start": v(0, -24.54) * mm, "end": v(-3.55, -17.84) * mm});
            skLineSegment(sketch, "E180", {"start": v(-3.55, -17.84) * mm, "end": v(-9.4, -22.67) * mm});
            skLineSegment(sketch, "E181", {"start": v(-9.4, -22.67) * mm, "end": v(-10.1, -15.13) * mm});
            skLineSegment(sketch, "E182", {"start": v(-10.1, -15.13) * mm, "end": v(-17.35, -17.35) * mm});
            skLineSegment(sketch, "E183", {"start": v(-17.35, -17.35) * mm, "end": v(-15.13, -10.1) * mm});
            skLineSegment(sketch, "E184", {"start": v(-15.13, -10.1) * mm, "end": v(-22.67, -9.4) * mm});
            skLineSegment(sketch, "E185", {"start": v(-22.67, -9.4) * mm, "end": v(-17.84, -3.55) * mm});
            skLineSegment(sketch, "E186", {"start": v(-17.84, -3.55) * mm, "end": v(-24.54, 0) * mm});
            skLineSegment(sketch, "E187", {"start": v(-24.54, 0) * mm, "end": v(-17.84, 3.55) * mm});
            skLineSegment(sketch, "E188", {"start": v(-17.84, 3.55) * mm, "end": v(-22.67, 9.4) * mm});
            skLineSegment(sketch, "E189", {"start": v(-22.67, 9.4) * mm, "end": v(-15.13, 10.1) * mm});
            skLineSegment(sketch, "E190", {"start": v(-15.13, 10.1) * mm, "end": v(-17.35, 17.35) * mm});
            skLineSegment(sketch, "E191", {"start": v(-17.35, 17.35) * mm, "end": v(-10.1, 15.13) * mm});
            skLineSegment(sketch, "E192", {"start": v(-10.1, 15.13) * mm, "end": v(-9.4, 22.67) * mm});
            skLineSegment(sketch, "E193", {"start": v(-9.4, 22.67) * mm, "end": v(-3.55, 17.84) * mm});
            skLineSegment(sketch, "E194", {"start": v(-3.55, 17.84) * mm, "end": v(0, 24.54) * mm});
            skSolve(sketch);
        }
        {
            var Q0;
            Q0 = qSketchRegion(id + "F8", true);
            var Q1;
            Q1 = qSketchRegion(id + "F6", true);
            extrude(context, id + "F7", {"entities" : qUnion([Q0, Q1]), "operationType" : NewBodyOperationType.ADD, "depth" : 6.35 * mm});
        }
        {
            var Q0;
            Q0=makeQuery(id+"F1.opExtrude","CAP_FACE",FACE,{"disambiguationData":[OSD([sQuery(id+"F0.wireOp",EDGE,"E0"),sQuery(id+"F0.wireOp",EDGE,"E62"),sQuery(id+"F0.wireOp",EDGE,"E63"),sQuery(id+"F0.wireOp",EDGE,"E64"),sQuery(id+"F0.wireOp",EDGE,"E65"),sQuery(id+"F0.wireOp",EDGE,"E66"),sQuery(id+"F0.wireOp",EDGE,"E67"),sQuery(id+"F0.wireOp",EDGE,"E68"),sQuery(id+"F0.wireOp",EDGE,"E69"),sQuery(id+"F0.wireOp",EDGE,"E70"),sQuery(id+"F0.wireOp",EDGE,"E71"),sQuery(id+"F0.wireOp",EDGE,"E72"),sQuery(id+"F0.wireOp",EDGE,"E73"),sQuery(id+"F0.wireOp",EDGE,"E74"),sQuery(id+"F0.wireOp",EDGE,"E75"),sQuery(id+"F0.wireOp",EDGE,"E76"),sQuery(id+"F0.wireOp",EDGE,"E77"),sQuery(id+"F0.wireOp",EDGE,"E78"),sQuery(id+"F0.wireOp",EDGE,"E79"),sQuery(id+"F0.wireOp",EDGE,"E80"),sQuery(id+"F0.wireOp",EDGE,"E81"),sQuery(id+"F0.wireOp",EDGE,"E82"),sQuery(id+"F0.wireOp",EDGE,"E83"),sQuery(id+"F0.wireOp",EDGE,"E84"),sQuery(id+"F0.wireOp",EDGE,"E85"),sQuery(id+"F0.wireOp",EDGE,"E86"),sQuery(id+"F0.wireOp",EDGE,"E87"),sQuery(id+"F0.wireOp",EDGE,"E88"),sQuery(id+"F0.wireOp",EDGE,"E89"),sQuery(id+"F0.wireOp",EDGE,"E90"),sQuery(id+"F0.wireOp",EDGE,"E91"),sQuery(id+"F0.wireOp",EDGE,"E92"),sQuery(id+"F0.wireOp",EDGE,"E93"),sQuery(id+"F0.wireOp",EDGE,"E94"),sQuery(id+"F0.wireOp",EDGE,"E95"),sQuery(id+"F0.wireOp",EDGE,"E96"),sQuery(id+"F0.wireOp",EDGE,"E97"),sQuery(id+"F0.wireOp",EDGE,"E98"),sQuery(id+"F0.wireOp",EDGE,"E99"),sQuery(id+"F0.wireOp",EDGE,"E100"),sQuery(id+"F0.wireOp",EDGE,"E101"),sQuery(id+"F0.wireOp",EDGE,"E102"),sQuery(id+"F0.wireOp",EDGE,"E103"),sQuery(id+"F0.wireOp",EDGE,"E104"),sQuery(id+"F0.wireOp",EDGE,"E105"),sQuery(id+"F0.wireOp",EDGE,"E106"),sQuery(id+"F0.wireOp",EDGE,"E107"),sQuery(id+"F0.wireOp",EDGE,"E108"),sQuery(id+"F0.wireOp",EDGE,"E109"),sQuery(id+"F0.wireOp",EDGE,"E110"),sQuery(id+"F0.wireOp",EDGE,"E111"),sQuery(id+"F0.wireOp",EDGE,"E112"),sQuery(id+"F0.wireOp",EDGE,"E113"),sQuery(id+"F0.wireOp",EDGE,"E114"),sQuery(id+"F0.wireOp",EDGE,"E115"),sQuery(id+"F0.wireOp",EDGE,"E116"),sQuery(id+"F0.wireOp",EDGE,"E117"),sQuery(id+"F0.wireOp",EDGE,"E118"),sQuery(id+"F0.wireOp",EDGE,"E120")])],"isStart":false});
            var sketch = newSketch(context, id + "F8", { "sketchPlane" : qUnion([Q0])});
            skCircle(sketch, "E195", {"center": v(0, 0) * mm, "radius": 3.18 * mm});
            skSolve(sketch);
        }
        {
            var Q0;
            Q0=makeQuery(id+"F8.imprint","IMPRINT",FACE,{"disambiguationData":[TD([[makeQuery(id+"F8.imprint","IMPRINT",EDGE,{"derivedFrom":sQuery(id+"F8.wireOp",EDGE,"E195")}),1.0]])]});
            extrude(context, id + "F9", {"entities" : qUnion([Q0]), "operationType" : NewBodyOperationType.REMOVE, "endBound" : BoundingType.THROUGH_ALL, "oppositeDirection" : true, "depth" : 25.4 * mm});
        }
        {
            var Q0;
            Q0 = qSketchRegion(id + "F8", true);
            extrude(context, id + "F10", {"entities" : qUnion([Q0]), "operationType" : NewBodyOperationType.REMOVE, "endBound" : BoundingType.THROUGH_ALL, "depth" : 25.4 * mm});
        }
    });
